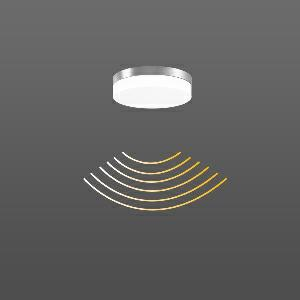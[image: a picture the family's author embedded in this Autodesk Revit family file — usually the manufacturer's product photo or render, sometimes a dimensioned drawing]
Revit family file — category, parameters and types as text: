
# Revit family: flat_slim_round_312135_004_3_191_eebc
name_source: partatom
category: Lighting Fixtures
units: mm (PartAtom-declared; Revit-internal decimal feet)

## family parameters
Cut with Voids When Loaded = No
Host = Face
Light Source = No
Part Type = Normal
Room Calculation Point = No
Round Connector Dimension = Use Diameter
Shared = No

## types (1)
- FLAT SLIM round (1 x LED Modul 840, 1300 lm, 4000)
    Apparent Load = 13 VA
    CIE Flux Codes = 43 74 92 91 100
    Color Rendering = 80
    Color Temperature = 4000
    Default Elevation = 1800 mm
    Height = 63 mm
    Lamp = 1 x LED Modul 840
    Lamp Light Flux = 1300 lm
    Lamp count = 1
    Length = 230 mm
    Lifetime = 50000 h
    Luminous efficacy = 100 lm/W
    Manufacturer = RZB
    ModVariant = No
    Model = 312135.004.3.191
    Mounting Place = Ceiling, Wall
    Mounting Type = Surface mounted
    Number of Poles = 1
    OnlyDefault = Yes
    Power Factor = 1
    Product Name = FLAT SLIM round
    Product group = Surface mounted ceiling and wall luminaires
    ProductGroupID = 305
    Protection Class = Protection class I
    Protection Degree = IP 65
    RLX_Detail_Level = 1
    RLX_Emergency_Light_Flux = 0 lm
    RLX_Emergency_Type = 0
    RLX_Emergency_Type_DB = No
    RlxData = <blob elided: 31393 chars, md5=c84caf64>
    Socket = socket
    Standby Power = 0 W
    System Light Flux = 1300 lm
    System Power = 13 W
    Type Comments = Product without accessories
    Type Image = 312132.004.19.jpg
    URL = http://relux.com
    VarID = ---
    Voltage = 230 V
    Voltage Range = 220-240 V
    Weight = 0.00 kg
    Width = 0 mm  [stored 0 ft]

note: [stored X ft] marks values corroborated as IEEE doubles in the binary element streams (Revit-internal decimal feet)

## geometry (parser evidence)
native form markers: Blend x4, Sweep x13
no freeform markers — native parametric forms only
